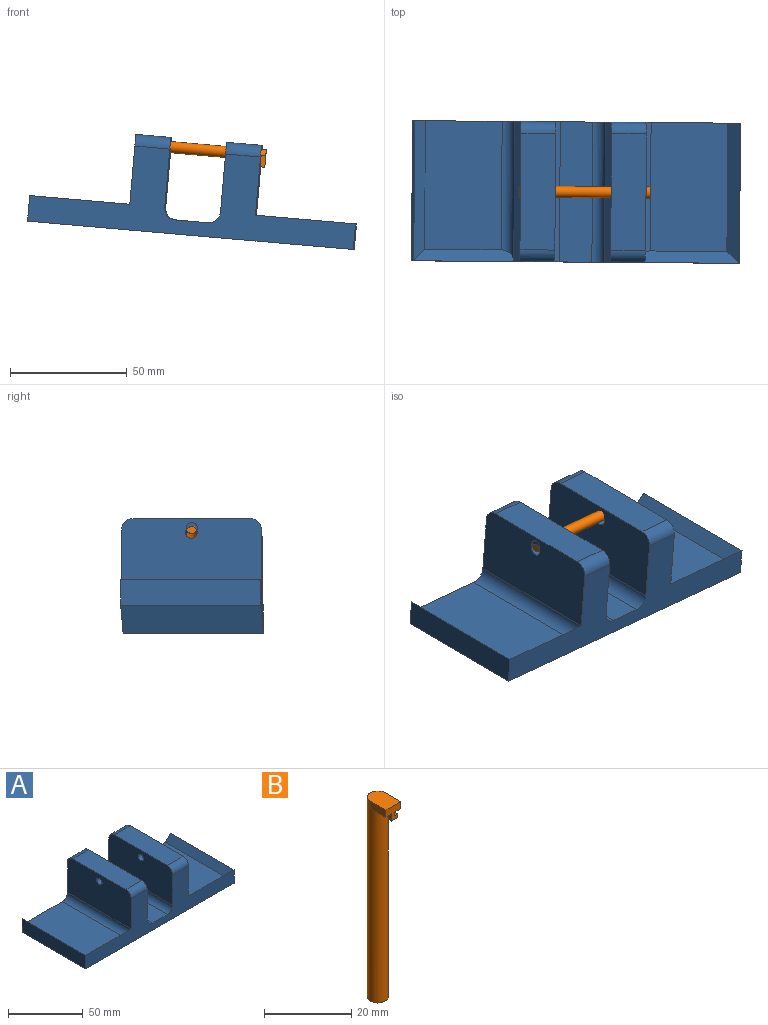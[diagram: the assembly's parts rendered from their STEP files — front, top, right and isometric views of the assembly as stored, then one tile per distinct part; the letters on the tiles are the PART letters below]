
ASSEMBLY  parts=2 mates=1
PART A: 37 faces, bbox 140x60x41 mm
  f0: plane 60x30mm, normal (1,0,0), area 1760.5mm2, adj f3,f5,f13,f14,f21,f22,f23,f28
  f1: plane 55x33mm, normal (0,0,1), area 1815mm2, adj f5,f18,f19,f25
  f2: plane 55x33mm, normal (0,0,1), area 1815mm2, adj f5,f16,f17,f21
  f3: plane 140x36mm, normal (0,-1,0), area 2180.7mm2, adj f0,f4,f6,f7,f8,f9,f10,f12
  f4: plane 60x11mm, normal (1,0,0), area 660mm2, adj f3,f5,f8,f17
  f5: plane 140x36mm, normal (0,1,0), area 1786.5mm2, adj f0,f1,f2,f4,f6,f7,f8,f9
  f6: plane 60x11mm, normal (-1,0,0), area 660mm2, adj f3,f5,f8,f18
  f7: plane 60x14mm, normal (0,0,1), area 840mm2, adj f3,f5,f20,f24
  f8: plane 140x60mm, normal (0,0,-1), area 8400mm2, adj f3,f4,f5,f6
  f9: plane 60x30mm, normal (-1,0,0), area 1769.6mm2, adj f3,f5,f11,f15,f25,f26,f27
  f10: plane 60x30mm, normal (1,0,0), area 1769.6mm2, adj f3,f5,f11,f15,f24,f26,f27
  f11: plane 50x15mm, normal (0,0,1), area 750mm2, adj f9,f10,f26,f27
  f12: plane 60x30mm, normal (-1,0,0), area 1769.6mm2, adj f3,f5,f13,f14,f20,f22,f23
  f13: plane 50x15mm, normal (0,0,1), area 750mm2, adj f0,f12,f22,f23
  f14: cylinder r=2.5mm len=15mm, axis (1,0,0), area 235.6mm2, adj f0,f12
  f15: cylinder r=2.5mm len=15mm, axis (1,0,0), area 235.6mm2, adj f9,f10
  f16: plane 43x5mm, normal (0,0.71,0.71), area 278.8mm2, adj f2,f3,f17,f21
  f17: plane 60x5mm, normal (-0.71,0,0.71), area 406.6mm2, adj f2,f4,f5,f16
  f18: plane 60x5mm, normal (0.71,0,0.71), area 406.6mm2, adj f1,f5,f6,f19
  f19: plane 43x5mm, normal (0,0.71,0.71), area 278.8mm2, adj f1,f3,f18,f25
  f20: cylinder r=5mm len=60mm, axis (0,-1,0), area 471.2mm2, adj f3,f5,f7,f12
  f21: cylinder r=5mm len=60mm, axis (0,1,0), area 446.2mm2, adj f0,f2,f5,f16
  f22: cylinder r=5mm len=15mm, axis (-1,0,0), area 117.8mm2, adj f0,f3,f12,f13
  f23: cylinder r=5mm len=15mm, axis (1,0,0), area 117.8mm2, adj f0,f5,f12,f13
  f24: cylinder r=5mm len=60mm, axis (0,1,0), area 471.2mm2, adj f3,f5,f7,f10
  f25: cylinder r=5mm len=60mm, axis (0,-1,0), area 446.2mm2, adj f1,f5,f9,f19
  f26: cylinder r=5mm len=15mm, axis (-1,0,0), area 117.8mm2, adj f3,f9,f10,f11
  f27: cylinder r=5mm len=15mm, axis (1,0,0), area 117.8mm2, adj f5,f9,f10,f11
  f28: cylinder r=4.05mm len=4.05mm, axis (-1,0,0), area 12.7mm2, adj f0,f30,f31,f32,f33
  f29: cylinder r=5.3mm len=5.3mm, axis (-1,0,0), area 16.7mm2, adj f0,f30,f31,f32,f34
  f30: plane 6.55x5.3mm, normal (1,0,0), area 10.7mm2, adj f28,f29,f32,f33,f34,f36
  f31: plane 1.25x0.75mm, normal (0,-1,0), area 0.9mm2, adj f0,f28,f29,f35
  f32: plane 2x1.25mm, normal (0,0,-1), area 2.5mm2, adj f0,f28,f29,f30
  f33: plane 1.25x1.25mm, normal (0,0,-1), area 1.6mm2, adj f28,f30,f35,f36
  f34: plane 1.25x1.25mm, normal (0,0,1), area 1.6mm2, adj f29,f30,f35,f36
  f35: plane 1.25x1.25mm, normal (-1,0,0), area 1.6mm2, adj f31,f33,f34,f36
  f36: plane 1.25x1.25mm, normal (0,-1,0), area 1.6mm2, adj f30,f33,f34,f35
PART B: 13 faces, bbox 4.8x7.4x56 mm
  f0: plane 5x4.75mm, normal (0,0,-1), area 13.9mm2, adj f1,f4,f5,f6,f7,f8,f12
  f1: cylinder r=2.38mm len=56mm, axis (0,0,-1), area 820.7mm2, adj f0,f2,f3,f4,f5
  f2: plane 7.38x4.75mm, normal (0,0,1), area 32.6mm2, adj f1,f4,f5,f6
  f3: plane 4.75x4.75mm, normal (0,0,-1), area 17.7mm2, adj f1
  f4: plane 5x2mm, normal (1,0,0), area 10mm2, adj f0,f1,f2,f6
  f5: plane 5x2mm, normal (-1,0,0), area 10mm2, adj f0,f1,f2,f6
  f6: plane 4.75x4mm, normal (0,-1,0), area 12.5mm2, adj f0,f2,f4,f5,f7,f8,f9,f10
  f7: plane 1x1mm, normal (1,0,0), area 1mm2, adj f0,f6,f11,f12
  f8: plane 2x1mm, normal (-1,0,0), area 2mm2, adj f0,f6,f9,f12
  f9: plane 2x1mm, normal (0,0,-1), area 2mm2, adj f6,f8,f10,f12
  f10: plane 1x1mm, normal (1,0,0), area 1mm2, adj f6,f9,f11,f12
  f11: plane 1x1mm, normal (0,0,1), area 1mm2, adj f6,f7,f10,f12
  f12: plane 2x2mm, normal (0,1,0), area 3mm2, adj f0,f7,f8,f9,f10,f11
PLACE A rot(axis=(0,1,-0.09),5deg) t=(-31.27,-2.09,6.3)mm
PLACE B rot(axis=(0.6,0.58,0.55),123.8deg) t=(-54.96,-1.97,45.36)mm
MATE pin_slot A.f28 <-> B.f1  axis (-1,0.01,0.09) through (-55.12,-1.9,43.51)mm
